# Revit family: Sanitary_Showers_AXOR_10637XXX-AXOR-ShowerSolutions-ShowerHeav_new
name_source: partatom
category: Plumbing Fixtures
revit_build: Autodesk Revit 2018 (Build: 20170223_1515(x64)
units: mm (PartAtom-declared; Revit-internal decimal feet)

## family parameters
Always vertical = No
Cut with Voids When Loaded = No
OmniClass Number = 23.31.17.00
OmniClass Title = Showers
Part Type = Normal
Room Calculation Point = No
Round Connector Dimension = Use Diameter
Shared = No
Work Plane-Based = Yes

## types (2) — shared parameters
Always visible = Yes
BIMobject category = Showers
Default Elevation = 1219.2 mm  [stored 4 ft]
Description = AXOR ShowerSolutions ShowerHeaven 1200/300 4jet without lighting
Design country = Germany
EAN code = 4059625030189
Edition number = 1
GTIN code = https://4059625030189
IFC Classification = Sanitary Terminal
Manufacturer = AXOR
Manufacturer country = Germany
Manufacturer name = AXOR
Masterformat 2014 Code = 22 41 23
Masterformat 2014 Description = Residential Showers
Model = 10637XXX
OmniClass Code = 23-31 17 00
OmniClass Description = Showers
Product Guid = 488f154a-585e-4c5c-ae93-608e0e7761ee
Product SKU = 10637XXX
Product data url = https://bimobject.com
Product family = AXOR ShowerSolutions
Product group = Overhead showers
Product name = 10637XXX AXOR ShowerSolutions ShowerHeaven 1200/300 4jet without lighting
Product url = https://www.axor-design.com
QR code = https://bimobject.com
UNSPSC Code = 30181503
URL = https://www.axor-design.com
Uniclass 2015 Code = Pr_40_20_87_76
Uniclass 2015 Name = Shower heads
Uniformat II Code = D2010
Uniformat II Description = Plumbing Fixtures
Weight Net (Kg) = 24.5

## per-type parameters (varying)
| type | Material 1 |
| 800 Stainless Steel Optic | AXOR - Metal - 800 Stainless Steel Optic |
| 330 Polished Black Chrome | AXOR - Metal - 330 Polished Black Chrome |

note: [stored X ft] marks values corroborated as IEEE doubles in the binary element streams (Revit-internal decimal feet)
